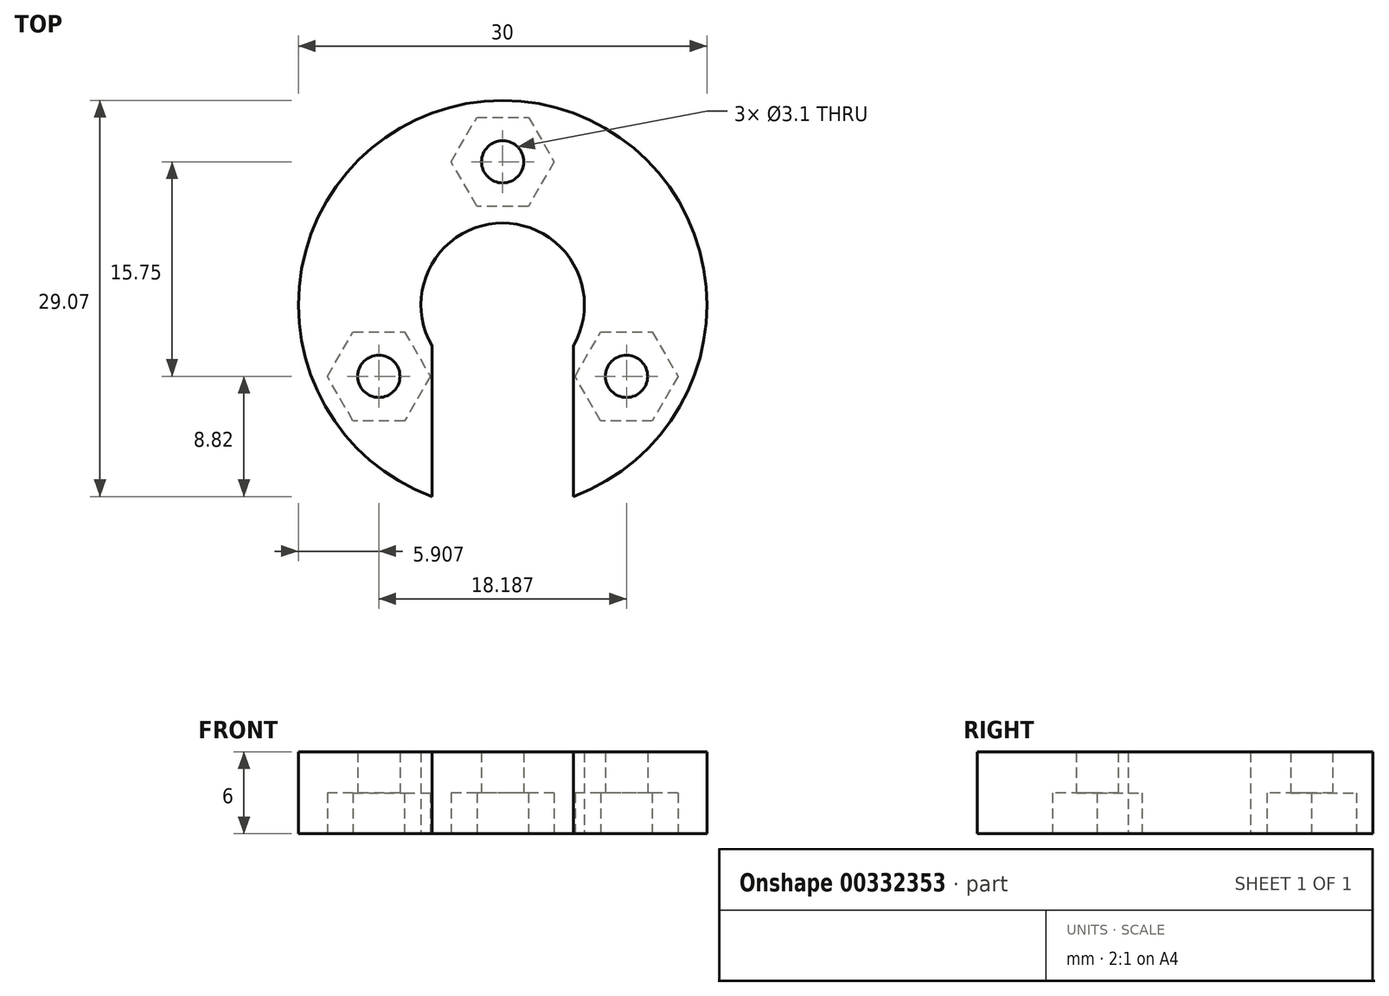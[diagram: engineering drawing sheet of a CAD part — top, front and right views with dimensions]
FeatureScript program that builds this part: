
annotation { "Feature Type Name" : "Feature", "Feature Type Description" : "" }
export const myFeature = defineFeature(function(context is Context, id is Id, definition is map)
    precondition{}
    {
        {
            var Q0;
            Q0=qCreatedBy(makeId("Top.planeOp"),FACE);
            var sketch = newSketch(context, id + "F0", { "sketchPlane" : qUnion([Q0])});
            skCircle(sketch, "E0", {"center": v(0, 0) * mm, "radius": 6 * mm});
            skCircle(sketch, "E1", {"center": v(0, 0) * mm, "radius": 15 * mm});
            skLineSegment(sketch, "E2", {"start": v(0, -6) * mm, "end": v(0, -15) * mm});
            skLineSegment(sketch, "E3.0", {"start": v(-5.2, -3) * mm, "end": v(-5.2, -14.07) * mm});
            skLineSegment(sketch, "E4.0", {"start": v(5.2, -3) * mm, "end": v(5.2, -14.07) * mm});
            skCircle(sketch, "E5", {"center": v(0, 10.5) * mm, "radius": 1.55 * mm});
            skCircle(sketch, "E6.1.0", {"center": v(-9.1, -5.25) * mm, "radius": 1.55 * mm});
            skCircle(sketch, "E6.2.0", {"center": v(9.1, -5.25) * mm, "radius": 1.55 * mm});
            skCircle(sketch, "E7.cCircle", {"center": v(0, 10.5) * mm, "radius": 3.27 * mm, "construction": true});
            skLineSegment(sketch, "E7.0", {"start": v(1.9, 7.22) * mm, "end": v(-1.9, 7.22) * mm});
            skLineSegment(sketch, "E7.1", {"start": v(-1.9, 7.23) * mm, "end": v(-3.78, 10.5) * mm});
            skLineSegment(sketch, "E7.2", {"start": v(-3.78, 10.5) * mm, "end": v(-1.9, 13.78) * mm});
            skLineSegment(sketch, "E7.3", {"start": v(-1.9, 13.78) * mm, "end": v(1.9, 13.78) * mm});
            skLineSegment(sketch, "E7.4", {"start": v(1.9, 13.78) * mm, "end": v(3.78, 10.5) * mm});
            skLineSegment(sketch, "E7.5", {"start": v(3.78, 10.5) * mm, "end": v(1.9, 7.22) * mm});
            skPoint(sketch, "E7.0.midPoint", {"position": v(0, 7.23) * mm});
            skLineSegment(sketch, "E8.1.0", {"start": v(-12.87, -5.25) * mm, "end": v(-10.98, -1.97) * mm});
            skLineSegment(sketch, "E8.1.1", {"start": v(-10.98, -8.52) * mm, "end": v(-12.87, -5.25) * mm});
            skLineSegment(sketch, "E8.1.2", {"start": v(-7.2, -8.53) * mm, "end": v(-10.98, -8.52) * mm});
            skLineSegment(sketch, "E8.1.3", {"start": v(-5.31, -5.25) * mm, "end": v(-7.2, -8.53) * mm});
            skLineSegment(sketch, "E8.1.4", {"start": v(-7.2, -1.97) * mm, "end": v(-5.31, -5.25) * mm});
            skLineSegment(sketch, "E8.1.5", {"start": v(-10.98, -1.97) * mm, "end": v(-7.2, -1.97) * mm});
            skLineSegment(sketch, "E8.2.0", {"start": v(10.98, -8.53) * mm, "end": v(7.2, -8.53) * mm});
            skLineSegment(sketch, "E8.2.1", {"start": v(12.87, -5.25) * mm, "end": v(10.98, -8.53) * mm});
            skLineSegment(sketch, "E8.2.2", {"start": v(10.98, -1.98) * mm, "end": v(12.87, -5.25) * mm});
            skLineSegment(sketch, "E8.2.3", {"start": v(7.2, -1.98) * mm, "end": v(10.98, -1.98) * mm});
            skLineSegment(sketch, "E8.2.4", {"start": v(5.31, -5.25) * mm, "end": v(7.2, -1.98) * mm});
            skLineSegment(sketch, "E8.2.5", {"start": v(7.2, -8.53) * mm, "end": v(5.31, -5.25) * mm});
            skSolve(sketch);
        }
        {
            var Q0;
            {var subQ0=sQuery(id+"F0.wireOp",EDGE,"E3.0");Q0=makeQuery(id+"F0.imprint","IMPRINT",FACE,{"disambiguationData":[TD([[makeQuery(id+"F0.imprint","IMPRINT",EDGE,{"derivedFrom":subQ0}),-1.0]])]});}
            extrude(context, id + "F1", {"entities" : qUnion([Q0]), "depth" : 6 * mm});
        }
        {
            var Q0;
            Q0=makeQuery(id+"F0.imprint","IMPRINT",FACE,{"disambiguationData":[TD([[makeQuery(id+"F0.imprint","IMPRINT",EDGE,{"derivedFrom":sQuery(id+"F0.wireOp",EDGE,"E6.2.0")}),-1.0]])]});
            var Q1;
            Q1=makeQuery(id+"F0.imprint","IMPRINT",FACE,{"disambiguationData":[TD([[makeQuery(id+"F0.imprint","IMPRINT",EDGE,{"derivedFrom":sQuery(id+"F0.wireOp",EDGE,"E5")}),-1.0]])]});
            var Q2;
            Q2=makeQuery(id+"F0.imprint","IMPRINT",FACE,{"disambiguationData":[TD([[makeQuery(id+"F0.imprint","IMPRINT",EDGE,{"derivedFrom":sQuery(id+"F0.wireOp",EDGE,"E6.1.0")}),-1.0]])]});
            extrude(context, id + "F2", {"entities" : qUnion([Q0, Q1, Q2]), "operationType" : NewBodyOperationType.ADD, "depth" : 6 * mm, "hasSecondDirection" : true, "secondDirectionOppositeDirection" : false, "secondDirectionDepth" : 3 * mm});
        }
    });
